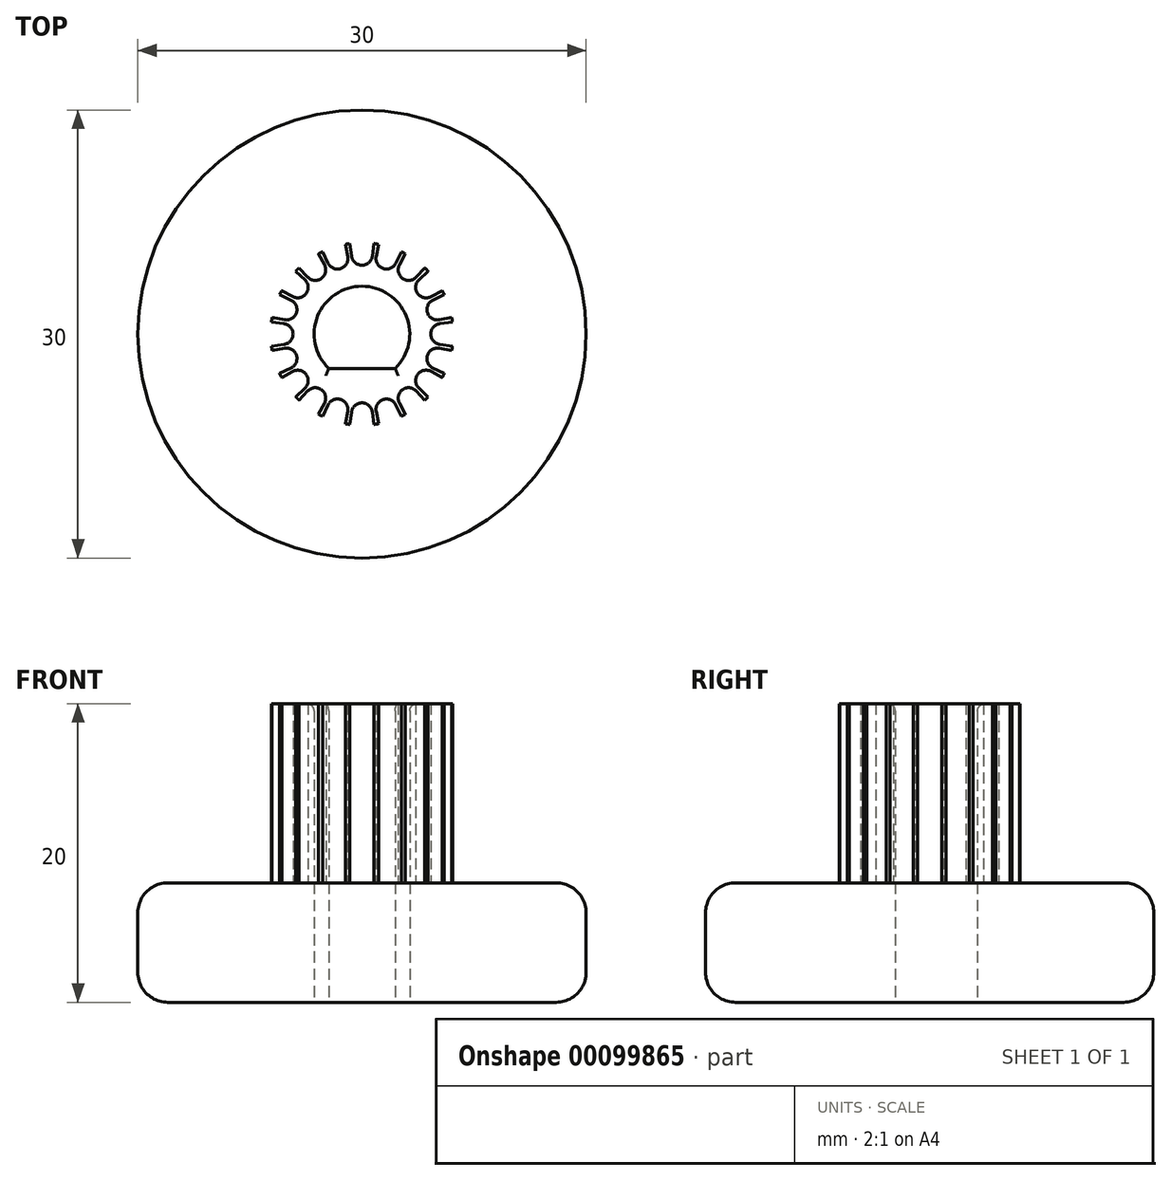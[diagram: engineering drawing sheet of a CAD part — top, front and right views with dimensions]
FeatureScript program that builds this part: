
annotation { "Feature Type Name" : "Feature", "Feature Type Description" : "" }
export const myFeature = defineFeature(function(context is Context, id is Id, definition is map)
    precondition{}
    {
        {
            var Q0;
            Q0=qCreatedBy(makeId("Top.planeOp"),FACE);
            var sketch = newSketch(context, id + "F0", { "sketchPlane" : qUnion([Q0])});
            skCircle(sketch, "E0", {"center": v(0, 0) * mm, "radius": 6.37 * mm, "construction": true});
            skCircle(sketch, "E1", {"center": v(0, 0) * mm, "radius": 6.11 * mm});
            skCircle(sketch, "E2", {"center": v(0, 0) * mm, "radius": 5.11 * mm, "construction": true});
            skLineSegment(sketch, "E3", {"start": v(0, 0) * mm, "end": v(0, 5.11) * mm, "construction": true});
            skLineSegment(sketch, "E4", {"start": v(0, 5.11) * mm, "end": v(0, 6.11) * mm, "construction": true});
            skArc(sketch, "E5", {"start": v(-0.7, 5.22) * mm, "mid": v(0, 4.61) * mm, "end": v(0.7, 5.22) * mm});
            skLineSegment(sketch, "E6", {"start": v(0.7, 5.22) * mm, "end": v(0.8, 6.06) * mm});
            skLineSegment(sketch, "E7", {"start": v(-0.7, 5.22) * mm, "end": v(-0.8, 6.06) * mm});
            skLineSegment(sketch, "E8.1.0", {"start": v(-2.27, 4.75) * mm, "end": v(-2.64, 5.51) * mm});
            skArc(sketch, "E8.1.1", {"start": v(-2.27, 4.75) * mm, "mid": v(-1.42, 4.38) * mm, "end": v(-0.95, 5.18) * mm});
            skLineSegment(sketch, "E8.1.2", {"start": v(-0.95, 5.18) * mm, "end": v(-1.1, 6) * mm});
            skLineSegment(sketch, "E8.2.0", {"start": v(-3.63, 3.81) * mm, "end": v(-4.21, 4.43) * mm});
            skArc(sketch, "E8.2.1", {"start": v(-3.63, 3.81) * mm, "mid": v(-2.7, 3.73) * mm, "end": v(-2.5, 4.63) * mm});
            skLineSegment(sketch, "E8.2.2", {"start": v(-2.5, 4.63) * mm, "end": v(-2.9, 5.37) * mm});
            skLineSegment(sketch, "E9.1.3.0", {"start": v(-4.63, 2.5) * mm, "end": v(-5.37, 2.9) * mm});
            skArc(sketch, "E9.3.3.0", {"start": v(-4.63, 2.5) * mm, "mid": v(-3.73, 2.7) * mm, "end": v(-3.81, 3.63) * mm});
            skLineSegment(sketch, "E9.7.3.0", {"start": v(-3.81, 3.63) * mm, "end": v(-4.43, 4.21) * mm});
            skLineSegment(sketch, "E9.1.4.0", {"start": v(-5.18, 0.95) * mm, "end": v(-6, 1.1) * mm});
            skArc(sketch, "E9.3.4.0", {"start": v(-5.18, 0.95) * mm, "mid": v(-4.38, 1.42) * mm, "end": v(-4.75, 2.27) * mm});
            skLineSegment(sketch, "E9.7.4.0", {"start": v(-4.75, 2.27) * mm, "end": v(-5.51, 2.64) * mm});
            skLineSegment(sketch, "E9.1.5.0", {"start": v(-5.22, -0.7) * mm, "end": v(-6.06, -0.8) * mm});
            skArc(sketch, "E9.3.5.0", {"start": v(-5.22, -0.7) * mm, "mid": v(-4.61, 0) * mm, "end": v(-5.22, 0.7) * mm});
            skLineSegment(sketch, "E9.7.5.0", {"start": v(-5.22, 0.7) * mm, "end": v(-6.06, 0.8) * mm});
            skLineSegment(sketch, "E9.1.6.0", {"start": v(-4.75, -2.27) * mm, "end": v(-5.51, -2.64) * mm});
            skArc(sketch, "E9.3.6.0", {"start": v(-4.75, -2.27) * mm, "mid": v(-4.38, -1.42) * mm, "end": v(-5.18, -0.95) * mm});
            skLineSegment(sketch, "E9.7.6.0", {"start": v(-5.18, -0.95) * mm, "end": v(-6, -1.1) * mm});
            skLineSegment(sketch, "E9.1.7.0", {"start": v(-3.81, -3.63) * mm, "end": v(-4.43, -4.21) * mm});
            skArc(sketch, "E9.3.7.0", {"start": v(-3.81, -3.63) * mm, "mid": v(-3.73, -2.7) * mm, "end": v(-4.63, -2.5) * mm});
            skLineSegment(sketch, "E9.7.7.0", {"start": v(-4.63, -2.5) * mm, "end": v(-5.37, -2.9) * mm});
            skLineSegment(sketch, "E9.1.8.0", {"start": v(-2.5, -4.63) * mm, "end": v(-2.9, -5.37) * mm});
            skArc(sketch, "E9.3.8.0", {"start": v(-2.5, -4.63) * mm, "mid": v(-2.7, -3.73) * mm, "end": v(-3.63, -3.81) * mm});
            skLineSegment(sketch, "E9.7.8.0", {"start": v(-3.63, -3.81) * mm, "end": v(-4.21, -4.43) * mm});
            skLineSegment(sketch, "E9.1.9.0", {"start": v(-0.95, -5.18) * mm, "end": v(-1.1, -6) * mm});
            skArc(sketch, "E9.3.9.0", {"start": v(-0.95, -5.18) * mm, "mid": v(-1.42, -4.38) * mm, "end": v(-2.27, -4.75) * mm});
            skLineSegment(sketch, "E9.7.9.0", {"start": v(-2.27, -4.75) * mm, "end": v(-2.64, -5.51) * mm});
            skLineSegment(sketch, "E9.1.10.0", {"start": v(0.7, -5.22) * mm, "end": v(0.8, -6.06) * mm});
            skArc(sketch, "E9.3.10.0", {"start": v(0.7, -5.22) * mm, "mid": v(0, -4.61) * mm, "end": v(-0.7, -5.22) * mm});
            skLineSegment(sketch, "E9.7.10.0", {"start": v(-0.7, -5.22) * mm, "end": v(-0.8, -6.06) * mm});
            skLineSegment(sketch, "E9.1.11.0", {"start": v(2.27, -4.75) * mm, "end": v(2.64, -5.51) * mm});
            skArc(sketch, "E9.3.11.0", {"start": v(2.27, -4.75) * mm, "mid": v(1.42, -4.38) * mm, "end": v(0.95, -5.18) * mm});
            skLineSegment(sketch, "E9.7.11.0", {"start": v(0.95, -5.18) * mm, "end": v(1.1, -6) * mm});
            skLineSegment(sketch, "E9.1.12.0", {"start": v(3.63, -3.81) * mm, "end": v(4.21, -4.43) * mm});
            skArc(sketch, "E9.3.12.0", {"start": v(3.63, -3.81) * mm, "mid": v(2.7, -3.73) * mm, "end": v(2.5, -4.63) * mm});
            skLineSegment(sketch, "E9.7.12.0", {"start": v(2.5, -4.63) * mm, "end": v(2.9, -5.37) * mm});
            skLineSegment(sketch, "E9.1.13.0", {"start": v(4.63, -2.5) * mm, "end": v(5.37, -2.9) * mm});
            skArc(sketch, "E9.3.13.0", {"start": v(4.63, -2.5) * mm, "mid": v(3.73, -2.7) * mm, "end": v(3.81, -3.63) * mm});
            skLineSegment(sketch, "E9.7.13.0", {"start": v(3.81, -3.63) * mm, "end": v(4.43, -4.21) * mm});
            skLineSegment(sketch, "E9.1.14.0", {"start": v(5.18, -0.95) * mm, "end": v(6, -1.1) * mm});
            skArc(sketch, "E9.3.14.0", {"start": v(5.18, -0.95) * mm, "mid": v(4.38, -1.42) * mm, "end": v(4.75, -2.27) * mm});
            skLineSegment(sketch, "E9.7.14.0", {"start": v(4.75, -2.27) * mm, "end": v(5.51, -2.64) * mm});
            skLineSegment(sketch, "E9.1.15.0", {"start": v(5.22, 0.7) * mm, "end": v(6.06, 0.8) * mm});
            skArc(sketch, "E9.3.15.0", {"start": v(5.22, 0.7) * mm, "mid": v(4.61, 0) * mm, "end": v(5.22, -0.7) * mm});
            skLineSegment(sketch, "E9.7.15.0", {"start": v(5.22, -0.7) * mm, "end": v(6.06, -0.8) * mm});
            skLineSegment(sketch, "E9.1.16.0", {"start": v(4.75, 2.27) * mm, "end": v(5.51, 2.64) * mm});
            skArc(sketch, "E9.3.16.0", {"start": v(4.75, 2.27) * mm, "mid": v(4.38, 1.42) * mm, "end": v(5.18, 0.95) * mm});
            skLineSegment(sketch, "E9.7.16.0", {"start": v(5.18, 0.95) * mm, "end": v(6, 1.1) * mm});
            skLineSegment(sketch, "E9.1.17.0", {"start": v(3.81, 3.63) * mm, "end": v(4.43, 4.21) * mm});
            skArc(sketch, "E9.3.17.0", {"start": v(3.81, 3.63) * mm, "mid": v(3.73, 2.7) * mm, "end": v(4.63, 2.5) * mm});
            skLineSegment(sketch, "E9.7.17.0", {"start": v(4.63, 2.5) * mm, "end": v(5.37, 2.9) * mm});
            skLineSegment(sketch, "E9.1.18.0", {"start": v(2.5, 4.63) * mm, "end": v(2.9, 5.37) * mm});
            skArc(sketch, "E9.3.18.0", {"start": v(2.5, 4.63) * mm, "mid": v(2.7, 3.73) * mm, "end": v(3.63, 3.81) * mm});
            skLineSegment(sketch, "E9.7.18.0", {"start": v(3.63, 3.81) * mm, "end": v(4.21, 4.43) * mm});
            skLineSegment(sketch, "E9.1.19.0", {"start": v(0.95, 5.18) * mm, "end": v(1.1, 6) * mm});
            skArc(sketch, "E9.3.19.0", {"start": v(0.95, 5.18) * mm, "mid": v(1.42, 4.38) * mm, "end": v(2.27, 4.75) * mm});
            skLineSegment(sketch, "E9.7.19.0", {"start": v(2.27, 4.75) * mm, "end": v(2.64, 5.51) * mm});
            skCircle(sketch, "E10", {"center": v(0, 0) * mm, "radius": 15 * mm});
            skArc(sketch, "E11", {"start": v(2.22, -2.3) * mm, "mid": v(0, 3.2) * mm, "end": v(-2.22, -2.3) * mm});
            skLineSegment(sketch, "E12", {"start": v(-2.22, -2.3) * mm, "end": v(2.22, -2.3) * mm});
            skSolve(sketch);
        }
        {
            var Q0;
            Q0=makeQuery(id+"F0.imprint","IMPRINT",FACE,{"disambiguationData":[TD([[makeQuery(id+"F0.imprint","IMPRINT",EDGE,{"derivedFrom":sQuery(id+"F0.wireOp",EDGE,"E5")}),-1.0]])]});
            extrude(context, id + "F1", {"entities" : qUnion([Q0]), "depth" : 12 * mm});
        }
        {
            var Q0;
            Q0=makeQuery(id+"F0.imprint","IMPRINT",FACE,{"disambiguationData":[TD([[makeQuery(id+"F0.imprint","IMPRINT",EDGE,{"derivedFrom":sQuery(id+"F0.wireOp",EDGE,"E5")}),-1.0]])]});
            var Q1;
            Q1=makeQuery(id+"F0.imprint","IMPRINT",FACE,{"disambiguationData":[TD([[makeQuery(id+"F0.imprint","IMPRINT",EDGE,{"derivedFrom":sQuery(id+"F0.wireOp",EDGE,"E10")}),1.0]])]});
            var Q2;
            {var subQ0=sQuery(id+"F0.wireOp",EDGE,"E9.1.7.0");Q2=makeQuery(id+"F0.imprint","IMPRINT",FACE,{"disambiguationData":[TD([[makeQuery(id+"F0.imprint","IMPRINT",EDGE,{"derivedFrom":subQ0}),-1.0]])]});}
            var Q3;
            {var subQ0=sQuery(id+"F0.wireOp",EDGE,"E9.1.6.0");Q3=makeQuery(id+"F0.imprint","IMPRINT",FACE,{"disambiguationData":[TD([[makeQuery(id+"F0.imprint","IMPRINT",EDGE,{"derivedFrom":subQ0}),-1.0]])]});}
            var Q4;
            {var subQ0=sQuery(id+"F0.wireOp",EDGE,"E9.1.8.0");Q4=makeQuery(id+"F0.imprint","IMPRINT",FACE,{"disambiguationData":[TD([[makeQuery(id+"F0.imprint","IMPRINT",EDGE,{"derivedFrom":subQ0}),-1.0]])]});}
            var Q5;
            {var subQ0=sQuery(id+"F0.wireOp",EDGE,"E9.1.9.0");Q5=makeQuery(id+"F0.imprint","IMPRINT",FACE,{"disambiguationData":[TD([[makeQuery(id+"F0.imprint","IMPRINT",EDGE,{"derivedFrom":subQ0}),-1.0]])]});}
            var Q6;
            {var subQ0=sQuery(id+"F0.wireOp",EDGE,"E9.1.10.0");Q6=makeQuery(id+"F0.imprint","IMPRINT",FACE,{"disambiguationData":[TD([[makeQuery(id+"F0.imprint","IMPRINT",EDGE,{"derivedFrom":subQ0}),-1.0]])]});}
            var Q7;
            {var subQ0=sQuery(id+"F0.wireOp",EDGE,"E9.1.11.0");Q7=makeQuery(id+"F0.imprint","IMPRINT",FACE,{"disambiguationData":[TD([[makeQuery(id+"F0.imprint","IMPRINT",EDGE,{"derivedFrom":subQ0}),-1.0]])]});}
            var Q8;
            {var subQ0=sQuery(id+"F0.wireOp",EDGE,"E9.1.12.0");Q8=makeQuery(id+"F0.imprint","IMPRINT",FACE,{"disambiguationData":[TD([[makeQuery(id+"F0.imprint","IMPRINT",EDGE,{"derivedFrom":subQ0}),-1.0]])]});}
            var Q9;
            {var subQ0=sQuery(id+"F0.wireOp",EDGE,"E9.1.13.0");Q9=makeQuery(id+"F0.imprint","IMPRINT",FACE,{"disambiguationData":[TD([[makeQuery(id+"F0.imprint","IMPRINT",EDGE,{"derivedFrom":subQ0}),-1.0]])]});}
            var Q10;
            {var subQ0=sQuery(id+"F0.wireOp",EDGE,"E9.1.14.0");Q10=makeQuery(id+"F0.imprint","IMPRINT",FACE,{"disambiguationData":[TD([[makeQuery(id+"F0.imprint","IMPRINT",EDGE,{"derivedFrom":subQ0}),-1.0]])]});}
            var Q11;
            {var subQ0=sQuery(id+"F0.wireOp",EDGE,"E9.1.15.0");Q11=makeQuery(id+"F0.imprint","IMPRINT",FACE,{"disambiguationData":[TD([[makeQuery(id+"F0.imprint","IMPRINT",EDGE,{"derivedFrom":subQ0}),-1.0]])]});}
            var Q12;
            {var subQ0=sQuery(id+"F0.wireOp",EDGE,"E9.1.16.0");Q12=makeQuery(id+"F0.imprint","IMPRINT",FACE,{"disambiguationData":[TD([[makeQuery(id+"F0.imprint","IMPRINT",EDGE,{"derivedFrom":subQ0}),-1.0]])]});}
            var Q13;
            {var subQ0=sQuery(id+"F0.wireOp",EDGE,"E9.1.17.0");Q13=makeQuery(id+"F0.imprint","IMPRINT",FACE,{"disambiguationData":[TD([[makeQuery(id+"F0.imprint","IMPRINT",EDGE,{"derivedFrom":subQ0}),-1.0]])]});}
            var Q14;
            {var subQ0=sQuery(id+"F0.wireOp",EDGE,"E9.1.18.0");Q14=makeQuery(id+"F0.imprint","IMPRINT",FACE,{"disambiguationData":[TD([[makeQuery(id+"F0.imprint","IMPRINT",EDGE,{"derivedFrom":subQ0}),-1.0]])]});}
            var Q15;
            {var subQ0=sQuery(id+"F0.wireOp",EDGE,"E9.1.19.0");Q15=makeQuery(id+"F0.imprint","IMPRINT",FACE,{"disambiguationData":[TD([[makeQuery(id+"F0.imprint","IMPRINT",EDGE,{"derivedFrom":subQ0}),-1.0]])]});}
            var Q16;
            Q16=makeQuery(id+"F0.imprint","IMPRINT",FACE,{"disambiguationData":[TD([[makeQuery(id+"F0.imprint","IMPRINT",EDGE,{"derivedFrom":sQuery(id+"F0.wireOp",EDGE,"E5")}),1.0]])]});
            var Q17;
            {var subQ0=sQuery(id+"F0.wireOp",EDGE,"E8.1.0");Q17=makeQuery(id+"F0.imprint","IMPRINT",FACE,{"disambiguationData":[TD([[makeQuery(id+"F0.imprint","IMPRINT",EDGE,{"derivedFrom":subQ0}),-1.0]])]});}
            var Q18;
            {var subQ0=sQuery(id+"F0.wireOp",EDGE,"E8.2.0");Q18=makeQuery(id+"F0.imprint","IMPRINT",FACE,{"disambiguationData":[TD([[makeQuery(id+"F0.imprint","IMPRINT",EDGE,{"derivedFrom":subQ0}),-1.0]])]});}
            var Q19;
            {var subQ0=sQuery(id+"F0.wireOp",EDGE,"E9.1.3.0");Q19=makeQuery(id+"F0.imprint","IMPRINT",FACE,{"disambiguationData":[TD([[makeQuery(id+"F0.imprint","IMPRINT",EDGE,{"derivedFrom":subQ0}),-1.0]])]});}
            var Q20;
            {var subQ0=sQuery(id+"F0.wireOp",EDGE,"E9.1.4.0");Q20=makeQuery(id+"F0.imprint","IMPRINT",FACE,{"disambiguationData":[TD([[makeQuery(id+"F0.imprint","IMPRINT",EDGE,{"derivedFrom":subQ0}),-1.0]])]});}
            var Q21;
            {var subQ0=sQuery(id+"F0.wireOp",EDGE,"E9.1.5.0");Q21=makeQuery(id+"F0.imprint","IMPRINT",FACE,{"disambiguationData":[TD([[makeQuery(id+"F0.imprint","IMPRINT",EDGE,{"derivedFrom":subQ0}),-1.0]])]});}
            extrude(context, id + "F2", {"entities" : qUnion([Q0, Q1, Q2, Q3, Q4, Q5, Q6, Q7, Q8, Q9, Q10, Q11, Q12, Q13, Q14, Q15, Q16, Q17, Q18, Q19, Q20, Q21]), "operationType" : NewBodyOperationType.ADD, "oppositeDirection" : true, "depth" : 8 * mm});
        }
        {
            var Q0;
            Q0=makeQuery(id+"F2.opExtrude","CAP_EDGE",EDGE,{"disambiguationData":[OSD([sQuery(id+"F0.wireOp",EDGE,"E10")])],"isStart":true});
            var Q1;
            Q1=makeQuery(id+"F2.opExtrude","CAP_EDGE",EDGE,{"disambiguationData":[OSD([sQuery(id+"F0.wireOp",EDGE,"E10")])],"isStart":false});
            fillet(context, id + "F3", {"entities" : qUnion([Q0, Q1]), "radius" : 2 * mm, "tangentPropagation" : true, "allowEdgeOverflow" : false});
        }
        {
            var Q0;
            Q0=makeQuery(id+"F1.opExtrude","CAP_EDGE",EDGE,{"disambiguationData":[OSD([sQuery(id+"F0.wireOp",EDGE,"E11")])],"isStart":false});
            var Q1;
            Q1=makeQuery(id+"F1.opExtrude","CAP_EDGE",EDGE,{"disambiguationData":[OSD([sQuery(id+"F0.wireOp",EDGE,"E12")])],"isStart":false});
            fillet(context, id + "F4", {"entities" : qUnion([Q0, Q1]), "radius" : 0.5 * mm, "tangentPropagation" : true, "allowEdgeOverflow" : false});
        }
    });
